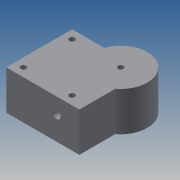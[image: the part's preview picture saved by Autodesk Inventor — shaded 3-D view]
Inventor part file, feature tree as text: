
AUTODESK INVENTOR PART (.ipt)
format: ipt  version: 2013 (Build 170138000, 138)  size: 114,688 bytes
history: native  units: mm
features: extrude x4, sketch x4
ambient origin geometry x8: Origin, YZ Plane, XZ Plane, XY Plane, X Axis, Y Axis, Z Axis, Center Point
bodies: Solid1 (feature_tree)
feature tree (8):
  extrude  "Extrusion1"  Depth=5.5mm
  extrude  "Extrusion2"  Depth=25.0mm TaperAngle=0.0deg
  extrude  "Extrusion3"  Depth=16.9mm
  extrude  "Extrusion4"  Depth=11.1mm
  sketch  "Sketch1"  dims[d0=42.0mm d1=5.5mm]
  sketch  "Sketch2"  dims[d2=3.5mm d3=25.0mm d4=0.0mm]
  sketch  "Sketch3"  dims[d5=4.6mm d6=0.0mm d7=16.9mm]
  sketch  "Sketch4"  dims[d9=4.6mm d10=0.0mm d11=11.1mm d12=15.0mm d13=6.0mm d14=10.0mm d15=0.0mm]
